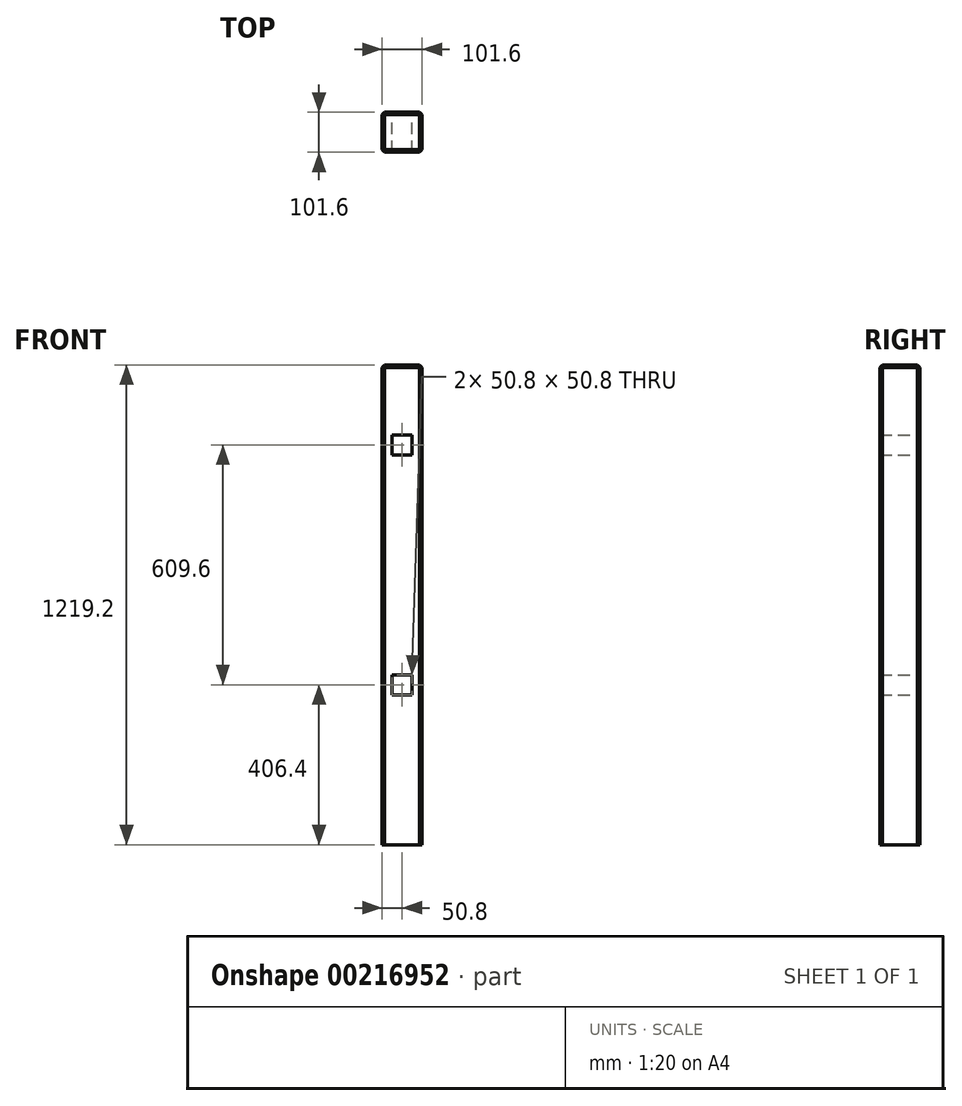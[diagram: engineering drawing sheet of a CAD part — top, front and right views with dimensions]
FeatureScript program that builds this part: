
annotation { "Feature Type Name" : "Feature", "Feature Type Description" : "" }
export const myFeature = defineFeature(function(context is Context, id is Id, definition is map)
    precondition{}
    {
        {
            var Q0;
            Q0=qCreatedBy(makeId("Front.planeOp"),FACE);
            var sketch = newSketch(context, id + "F0", { "sketchPlane" : qUnion([Q0])});
            skLineSegment(sketch, "E0.bottom", {"start": v(50.8, 609.6) * mm, "end": v(-50.8, 609.6) * mm});
            skLineSegment(sketch, "E0.top", {"start": v(50.8, -609.6) * mm, "end": v(-50.8, -609.6) * mm});
            skLineSegment(sketch, "E0.left", {"start": v(50.8, 609.6) * mm, "end": v(50.8, -609.6) * mm});
            skLineSegment(sketch, "E0.right", {"start": v(-50.8, 609.6) * mm, "end": v(-50.8, -609.6) * mm});
            skPoint(sketch, "E0.middle", {"position": v(0, 0) * mm});
            skLineSegment(sketch, "E1", {"start": v(50.8, -609.6) * mm, "end": v(50.8, -203.2) * mm});
            skLineSegment(sketch, "E2", {"start": v(-50.8, -203.2) * mm, "end": v(-50.8, 406.4) * mm});
            skLineSegment(sketch, "E3.bottom", {"start": v(25.4, 431.8) * mm, "end": v(-25.4, 431.8) * mm});
            skLineSegment(sketch, "E3.top", {"start": v(25.4, 381) * mm, "end": v(-25.4, 381) * mm});
            skLineSegment(sketch, "E3.left", {"start": v(25.4, 431.8) * mm, "end": v(25.4, 381) * mm});
            skLineSegment(sketch, "E3.right", {"start": v(-25.4, 431.8) * mm, "end": v(-25.4, 381) * mm});
            skPoint(sketch, "E3.middle", {"position": v(0, 406.4) * mm});
            skLineSegment(sketch, "E4.bottom", {"start": v(25.4, -177.8) * mm, "end": v(-25.4, -177.8) * mm});
            skLineSegment(sketch, "E4.top", {"start": v(25.4, -228.6) * mm, "end": v(-25.4, -228.6) * mm});
            skLineSegment(sketch, "E4.left", {"start": v(25.4, -177.8) * mm, "end": v(25.4, -228.6) * mm});
            skLineSegment(sketch, "E4.right", {"start": v(-25.4, -177.8) * mm, "end": v(-25.4, -228.6) * mm});
            skPoint(sketch, "E4.middle", {"position": v(0, -203.2) * mm});
            skSolve(sketch);
        }
        {
            var Q0;
            Q0 = qSketchRegion(id + "F0", true);
            extrude(context, id + "F1", {"entities" : qUnion([Q0]), "depth" : 101.6 * mm});
        }
        {
            var Q0;
            Q0=makeQuery(id+"F1.opExtrude","CAP_EDGE",EDGE,{"disambiguationData":[OSD([sQuery(id+"F0.wireOp",EDGE,"E0.right"),sQuery(id+"F0.wireOp",EDGE,"E2")])],"isStart":false});
            var Q1;
            Q1=makeQuery(id+"F1.opExtrude","CAP_EDGE",EDGE,{"disambiguationData":[OSD([sQuery(id+"F0.wireOp",EDGE,"E0.left"),sQuery(id+"F0.wireOp",EDGE,"E1")])],"isStart":false});
            var Q2;
            Q2=makeQuery(id+"F1.opExtrude","CAP_EDGE",EDGE,{"disambiguationData":[OSD([sQuery(id+"F0.wireOp",EDGE,"E0.left"),sQuery(id+"F0.wireOp",EDGE,"E1")])],"isStart":true});
            var Q3;
            Q3=makeQuery(id+"F1.opExtrude","CAP_EDGE",EDGE,{"disambiguationData":[OSD([sQuery(id+"F0.wireOp",EDGE,"E0.right"),sQuery(id+"F0.wireOp",EDGE,"E2")])],"isStart":true});
            var Q4;
            Q4=makeQuery(id+"F1.opExtrude","CAP_EDGE",EDGE,{"disambiguationData":[OSD([sQuery(id+"F0.wireOp",EDGE,"E0.bottom")])],"isStart":true});
            var Q5;
            Q5=makeQuery(id+"F1.opExtrude","SWEPT_EDGE",EDGE,{"disambiguationData":[OSD([sQuery(id+"F0.wireOp",EDGE,"E0.bottom"),sQuery(id+"F0.wireOp",EDGE,"E0.left")])]});
            var Q6;
            Q6=makeQuery(id+"F1.opExtrude","CAP_EDGE",EDGE,{"disambiguationData":[OSD([sQuery(id+"F0.wireOp",EDGE,"E0.bottom")])],"isStart":false});
            var Q7;
            Q7=makeQuery(id+"F1.opExtrude","SWEPT_EDGE",EDGE,{"disambiguationData":[OSD([sQuery(id+"F0.wireOp",EDGE,"E0.bottom"),sQuery(id+"F0.wireOp",EDGE,"E0.right")])]});
            chamfer(context, id + "F2", {"entities" : qUnion([Q0, Q1, Q2, Q3, Q4, Q5, Q6, Q7]), "width" : 6.35 * mm, "tangentPropagation" : true});
        }
    });
